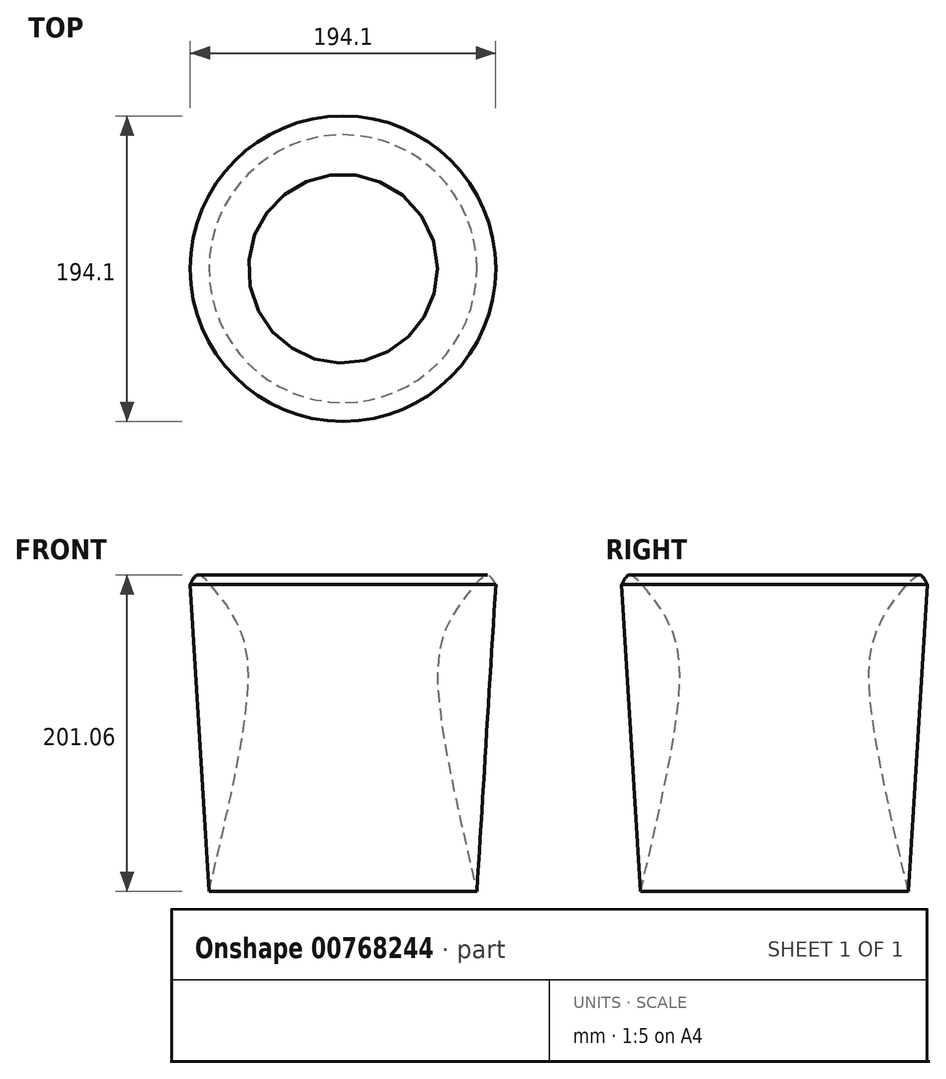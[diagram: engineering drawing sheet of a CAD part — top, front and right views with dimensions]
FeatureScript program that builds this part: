
annotation { "Feature Type Name" : "Feature", "Feature Type Description" : "" }
export const myFeature = defineFeature(function(context is Context, id is Id, definition is map)
    precondition{}
    {
        {
            var Q0;
            Q0=qCreatedBy(makeId("Front.planeOp"),FACE);
            var sketch = newSketch(context, id + "F0", { "sketchPlane" : qUnion([Q0])});
            skLineSegment(sketch, "E0", {"start": v(0, 131.2) * mm, "end": v(0, -104.1) * mm});
            skLineSegment(sketch, "E1", {"start": v(-97.05, 112.84) * mm, "end": v(-85.07, -82.17) * mm});
            skFitSpline(sketch, "E2", {"points": [v(-97.05, 112.84) * mm, v(-92.4, 118.84) * mm, v(-84.25, 112.84) * mm, v(-64.74, 83.12) * mm, v(-61.69, 32.16) * mm, v(-85.07, -82.17) * mm], "startDerivative": vector(45.67, 90.84) * mm, "endDerivative": vector(-80.85, -344.72) * mm});
            skFitSpline(sketch, "E3", {"points": [v(0, -31.48) * mm, v(-7.29, -5.79) * mm, v(-14.19, 35.99) * mm, v(-13.28, 52.05) * mm, v(-5.66, 59.93) * mm, v(0, 60.67) * mm], "startDerivative": vector(-30.82, 95.14) * mm, "endDerivative": vector(48.9, -0.38) * mm});
            skLineSegment(sketch, "E4", {"start": v(-23.66, 60.68) * mm, "end": v(28.93, 60.68) * mm});
            skLineSegment(sketch, "E5", {"start": v(0, -31.48) * mm, "end": v(0, 60.67) * mm});
            skSolve(sketch);
        }
        {
            var Q0;
            Q0=makeQuery(id+"F0.imprint","IMPRINT",FACE,{"disambiguationData":[TD([[makeQuery(id+"F0.imprint","IMPRINT",EDGE,{"derivedFrom":sQuery(id+"F0.wireOp",EDGE,"E1")}),1.0]])]});
            var Q1;
            {var subQ0=sQuery(id+"F0.wireOp",EDGE,"E5");Q1=makeQuery(id+"F0.imprint","IMPRINT",FACE,{"disambiguationData":[TD([[makeQuery(id+"F0.imprint","IMPRINT",EDGE,{"derivedFrom":subQ0}),1.0]])]});}
            var Q2;
            Q2=sQuery(id+"F0.wireOp",EDGE,"E0");
            revolve(context, id + "F1", {"surfaceOperationType" : NewSurfaceOperationType.NEW, "entities" : qUnion([Q0, Q1]), "axis" : qUnion([Q2]), "revolveType" : RevolveType.FULL});
        }
    });
